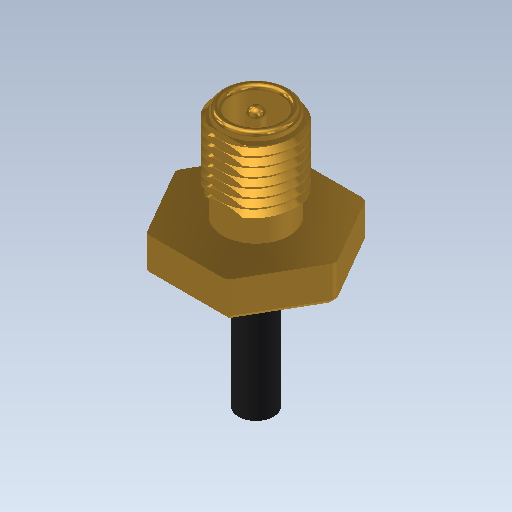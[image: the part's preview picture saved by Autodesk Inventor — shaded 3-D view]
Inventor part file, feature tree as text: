
AUTODESK INVENTOR PART (.ipt)
format: ipt  version: 2021 (Build 250183000, 183)  size: 485,888 bytes
history: native  units: mm
features: extrude x6, sketch x6, fillet x3, helix x1, chamfer x1, projected_geometry x1
ambient origin geometry x8: Origin, YZ Plane, XZ Plane, XY Plane, X Axis, Y Axis, Z Axis, Center Point
bodies: Solid1 (feature_tree), Solid2 (feature_tree), Solid3 (feature_tree)
feature tree (18):
  helix  "Coil1"  [1 undecoded]
  extrude  "Extrusion1"  Depth=2.63525mm
  extrude  "Extrusion2"  Depth=0.70612mm
  fillet  "Fillet1"  Radius=10.0mm
  fillet  "Fillet2"  Radius=5.0mm
  extrude  "Extrusion3"  Depth=2.0mm
  extrude  "Extrusion5"  Depth=1.27mm
  extrude  "Extrusion6"  Depth=0.35mm
  extrude  "Extrusion7"  Depth=2.0mm
  fillet  "Fillet3"  Radius=3.0mm
  chamfer  "Chamfer2"  Distance=1.27mm
  sketch  "Sketch2"  dims[d13=2.25mm d14=0.70612mm]
  sketch  "Sketch3"  dims[d15=8.0mm d16=10.0mm d17=0.0mm d18=90.0deg d19=90.0deg d20=0.0mm d21=0.0mm d24=10.0mm d25=0.0mm d26=5.0mm]
  projected_geometry  "Projected Loop1"
  sketch  "Sketch6"  dims[d27=8.0mm d28=2.0mm]
  sketch  "Sketch7"  dims[d29=0.75mm d30=1.27mm]
  sketch  "Sketch8"  dims[d31=7.6mm d32=0.0mm d33=0.35mm d34=0.6mm d41=3.0mm d42=0.0mm d56=1.27mm d57=0.0mm d64=6.4mm d65=5.85mm d66=10.0mm d67=0.0mm d74=11.0mm d75=10.0mm d76=0.0mm d77=0.5mm d78=0.5mm d79=2.0mm d80=45.0deg]
  sketch  "Sketch1"  dims[d9=3.09372mm d11=2.63525mm]
note: 1 required parameter value undecoded (feature->parameter linkage not recoverable at this tier; creation-order binding heuristic only, values carry confidence <= 0.55)
